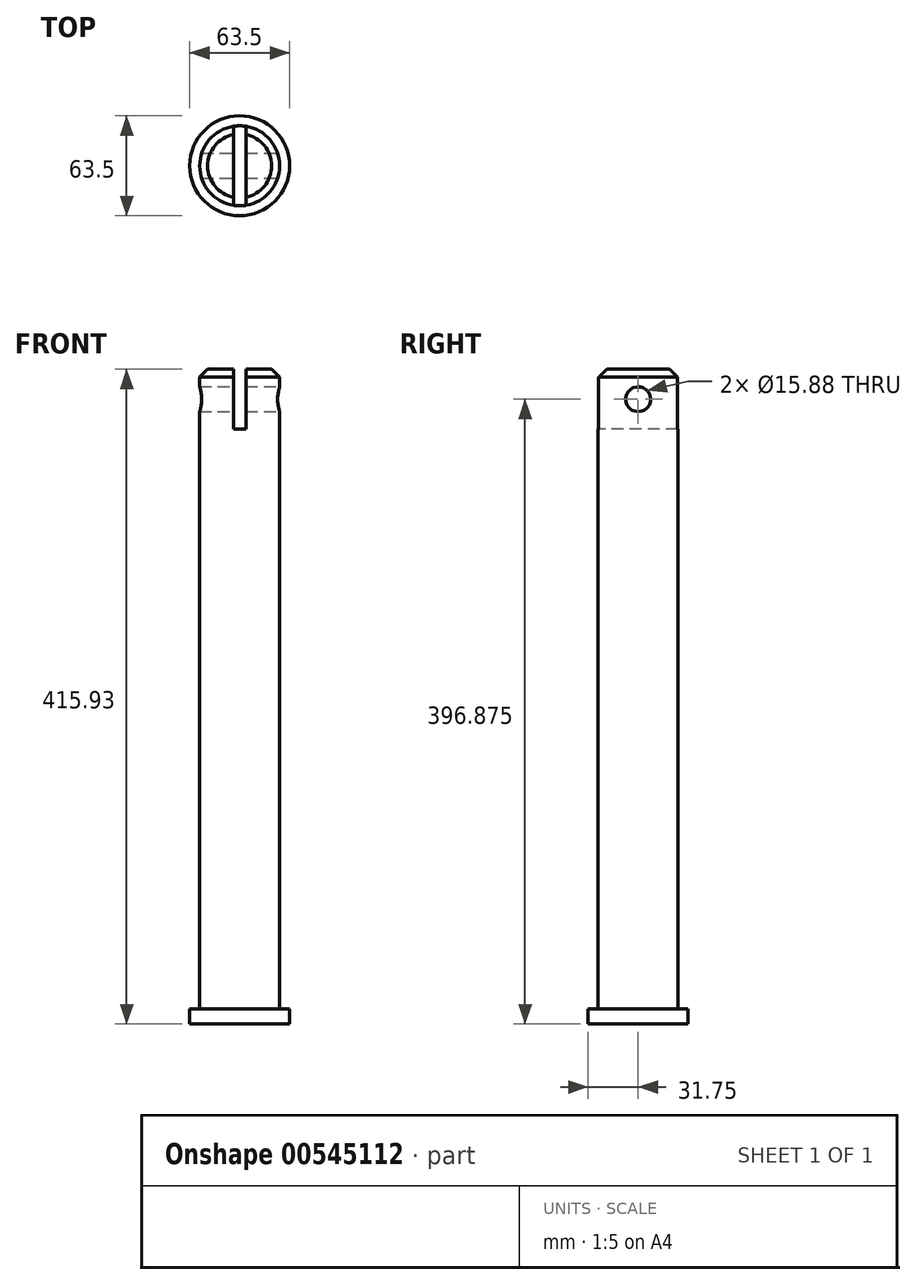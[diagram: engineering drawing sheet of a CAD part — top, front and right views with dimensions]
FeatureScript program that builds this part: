
annotation { "Feature Type Name" : "Feature", "Feature Type Description" : "" }
export const myFeature = defineFeature(function(context is Context, id is Id, definition is map)
    precondition{}
    {
        {
            var Q0;
            Q0=qCreatedBy(makeId("Top.planeOp"),FACE);
            var sketch = newSketch(context, id + "F0", { "sketchPlane" : qUnion([Q0])});
            skCircle(sketch, "E0", {"center": v(0, 0) * mm, "radius": 31.75 * mm});
            skSolve(sketch);
        }
        {
            var Q0;
            Q0=makeQuery(id+"F0.imprint","IMPRINT",FACE,{"disambiguationData":[TD([[makeQuery(id+"F0.imprint","IMPRINT",EDGE,{"derivedFrom":sQuery(id+"F0.wireOp",EDGE,"E0")}),1.0]])]});
            extrude(context, id + "F1", {"entities" : qUnion([Q0]), "depth" : 9.52 * mm, "offsetDistance" : 25.4 * mm});
        }
        {
            var Q0;
            Q0=makeQuery(id+"F1.opExtrude","CAP_FACE",FACE,{"disambiguationData":[OSD([sQuery(id+"F0.wireOp",EDGE,"E0")])],"isStart":false});
            var sketch = newSketch(context, id + "F2", { "sketchPlane" : qUnion([Q0])});
            skPoint(sketch, "E1", {"position": v(0, 0) * mm});
            skCircle(sketch, "E2", {"center": v(0, 0) * mm, "radius": 25.4 * mm});
            skSolve(sketch);
        }
        {
            var Q0;
            Q0=makeQuery(id+"F2.imprint","IMPRINT",FACE,{"disambiguationData":[TD([[makeQuery(id+"F2.imprint","IMPRINT",EDGE,{"derivedFrom":sQuery(id+"F2.wireOp",EDGE,"E2")}),1.0]])]});
            extrude(context, id + "F3", {"entities" : qUnion([Q0]), "operationType" : NewBodyOperationType.ADD, "depth" : 406.4 * mm, "offsetDistance" : 25.4 * mm});
        }
        {
            var Q0;
            Q0=makeQuery(id+"F3.opExtrude","CAP_FACE",FACE,{"disambiguationData":[OSD([sQuery(id+"F2.wireOp",EDGE,"E2")])],"isStart":false});
            var sketch = newSketch(context, id + "F4", { "sketchPlane" : qUnion([Q0])});
            skLineSegment(sketch, "E3.bottom", {"start": v(-3.97, 41.47) * mm, "end": v(3.97, 41.47) * mm});
            skLineSegment(sketch, "E3.top", {"start": v(-3.97, -41.47) * mm, "end": v(3.97, -41.47) * mm});
            skLineSegment(sketch, "E3.left", {"start": v(-3.97, 41.47) * mm, "end": v(-3.97, -41.47) * mm});
            skLineSegment(sketch, "E3.right", {"start": v(3.97, 41.47) * mm, "end": v(3.97, -41.47) * mm});
            skPoint(sketch, "E3.middle", {"position": v(0, 0) * mm});
            skSolve(sketch);
        }
        {
            var Q0;
            {var subQ0=sQuery(id+"F4.wireOp",EDGE,"E3.left");var subQ1=makeQuery(id+"F3.opExtrude","CAP_EDGE",EDGE,{"disambiguationData":[OSD([sQuery(id+"F2.wireOp",EDGE,"E2")])],"isStart":false});var subQ2=makeQuery(id+"F4.imprint","INTERSECT",VERTEX,{"disambiguationData":[OD(0.0)],"derivedFrom":[subQ1,subQ0]});Q0=makeQuery(id+"F4.imprint","IMPRINT",FACE,{"disambiguationData":[TD([[makeQuery(id+"F4.imprint","IMPRINT",EDGE,{"disambiguationData":[TD([[subQ2,-1.0]])],"derivedFrom":subQ0}),1.0]])]});}
            extrude(context, id + "F5", {"entities" : qUnion([Q0]), "operationType" : NewBodyOperationType.REMOVE, "oppositeDirection" : true, "depth" : 38.1 * mm, "offsetDistance" : 25.4 * mm});
        }
        {
            var Q0;
            Q0=makeQuery(id+"F5.boolean.opBoolean","COPY",FACE,{"derivedFrom":makeQuery(id+"F5.opExtrude","SWEPT_FACE",FACE,{"disambiguationData":[OSD([sQuery(id+"F4.wireOp",EDGE,"E3.left")])]})});
            var sketch = newSketch(context, id + "F6", { "sketchPlane" : qUnion([Q0])});
            skPoint(sketch, "E4", {"position": v(0, 396.88) * mm});
            skCircle(sketch, "E5", {"center": v(0, 396.88) * mm, "radius": 7.94 * mm});
            skSolve(sketch);
        }
        {
            var Q0;
            Q0 = qSketchRegion(id + "F6", true);
            extrude(context, id + "F7", {"entities" : qUnion([Q0]), "operationType" : NewBodyOperationType.REMOVE, "oppositeDirection" : true, "depth" : 25.4 * mm, "offsetDistance" : 25.4 * mm, "hasSecondDirection" : true, "secondDirectionOppositeDirection" : false, "secondDirectionDepth" : 50.8 * mm});
        }
        {
            var Q0;
            {var subQ0=sQuery(id+"F2.wireOp",EDGE,"E2");Q0=makeQuery(id+"F5.boolean.opBoolean","SPLIT",EDGE,{"disambiguationData":[TD([makeQuery(id+"F5.opExtrude","SWEPT_FACE",FACE,{"disambiguationData":[OSD([sQuery(id+"F4.wireOp",EDGE,"E3.right")])]})])],"derivedFrom":makeQuery(id+"F3.opExtrude","CAP_EDGE",EDGE,{"disambiguationData":[OSD([subQ0])],"isStart":false})});}
            var Q1;
            {var subQ0=sQuery(id+"F2.wireOp",EDGE,"E2");Q1=makeQuery(id+"F5.boolean.opBoolean","SPLIT",EDGE,{"disambiguationData":[TD([makeQuery(id+"F5.opExtrude","SWEPT_FACE",FACE,{"disambiguationData":[OSD([sQuery(id+"F4.wireOp",EDGE,"E3.left")])]})])],"derivedFrom":makeQuery(id+"F3.opExtrude","CAP_EDGE",EDGE,{"disambiguationData":[OSD([subQ0])],"isStart":false})});}
            chamfer(context, id + "F8", {"entities" : qUnion([Q0, Q1]), "width" : 5.08 * mm, "tangentPropagation" : true});
        }
    });
